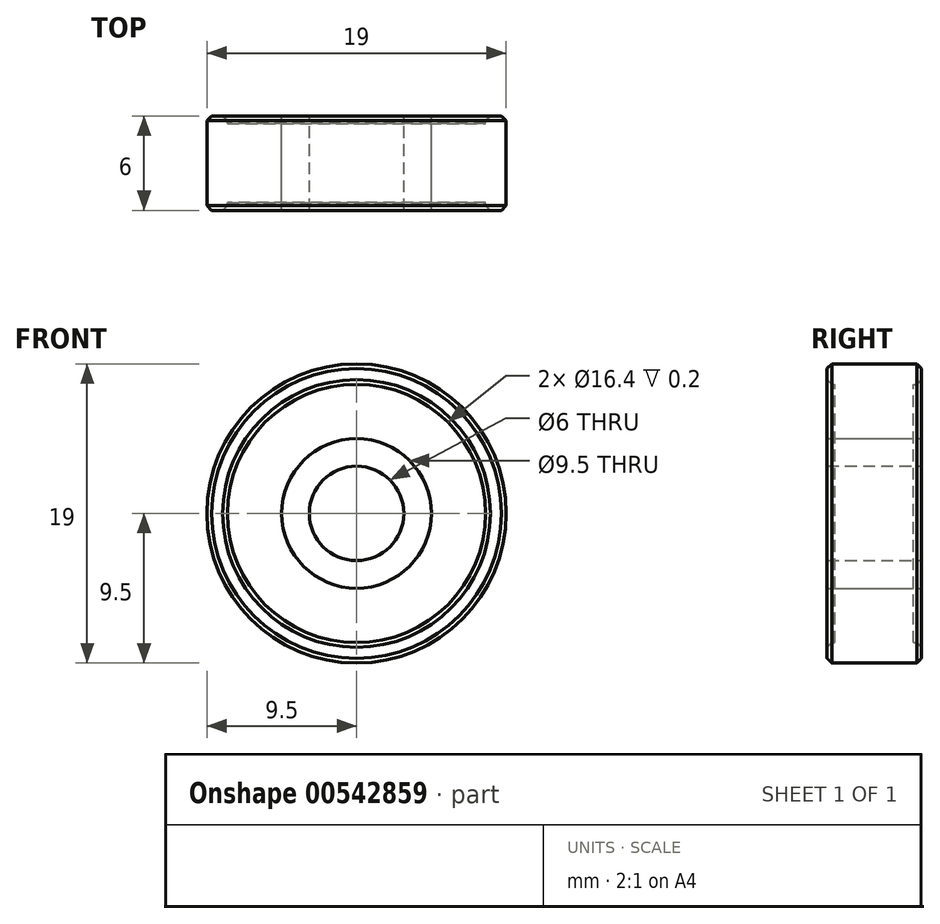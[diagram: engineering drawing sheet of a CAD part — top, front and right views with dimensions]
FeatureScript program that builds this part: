
annotation { "Feature Type Name" : "Feature", "Feature Type Description" : "" }
export const myFeature = defineFeature(function(context is Context, id is Id, definition is map)
    precondition{}
    {
        {
            var Q0;
            Q0=qCreatedBy(makeId("Front.planeOp"),FACE);
            var sketch = newSketch(context, id + "F0", { "sketchPlane" : qUnion([Q0])});
            skCircle(sketch, "E0", {"center": v(0, 0) * mm, "radius": 9.5 * mm});
            skCircle(sketch, "E1", {"center": v(0, 0) * mm, "radius": 8.2 * mm});
            skCircle(sketch, "E2", {"center": v(0, 0) * mm, "radius": 4.75 * mm});
            skCircle(sketch, "E3", {"center": v(0, 0) * mm, "radius": 3 * mm});
            skSolve(sketch);
        }
        {
            var Q0;
            Q0=makeQuery(id+"F0.imprint","IMPRINT",FACE,{"disambiguationData":[TD([[makeQuery(id+"F0.imprint","IMPRINT",EDGE,{"derivedFrom":sQuery(id+"F0.wireOp",EDGE,"E0")}),1.0]])]});
            extrude(context, id + "F1", {"entities" : qUnion([Q0]), "endBound" : BoundingType.SYMMETRIC, "depth" : 6 * mm, "offsetDistance" : 25 * mm});
        }
        {
            var Q0;
            Q0=makeQuery(id+"F0.imprint","IMPRINT",FACE,{"disambiguationData":[TD([[makeQuery(id+"F0.imprint","IMPRINT",EDGE,{"derivedFrom":sQuery(id+"F0.wireOp",EDGE,"E1")}),1.0]])]});
            extrude(context, id + "F2", {"entities" : qUnion([Q0]), "operationType" : NewBodyOperationType.ADD, "endBound" : BoundingType.SYMMETRIC, "depth" : 5 * mm});
        }
        {
            var Q0;
            Q0=makeQuery(id+"F1.opExtrude","CAP_FACE",FACE,{"disambiguationData":[OSD([sQuery(id+"F0.wireOp",EDGE,"E0"),sQuery(id+"F0.wireOp",EDGE,"E1")])],"isStart":false});
            var Q1;
            Q1=makeQuery(id+"F1.opExtrude","CAP_FACE",FACE,{"disambiguationData":[OSD([sQuery(id+"F0.wireOp",EDGE,"E2"),sQuery(id+"F0.wireOp",EDGE,"E3")])],"isStart":false});
            var Q2;
            Q2=makeQuery(id+"F1.opExtrude","CAP_FACE",FACE,{"disambiguationData":[OSD([sQuery(id+"F0.wireOp",EDGE,"E0"),sQuery(id+"F0.wireOp",EDGE,"E1")])],"isStart":true});
            var Q3;
            Q3=makeQuery(id+"F1.opExtrude","CAP_FACE",FACE,{"disambiguationData":[OSD([sQuery(id+"F0.wireOp",EDGE,"E2"),sQuery(id+"F0.wireOp",EDGE,"E3")])],"isStart":true});
            chamfer(context, id + "F3", {"entities" : qUnion([Q0, Q1, Q2, Q3]), "width" : .3 * mm, "tangentPropagation" : true});
        }
        {
            var Q0;
            Q0=makeQuery(id+"F0.imprint","IMPRINT",FACE,{"disambiguationData":[TD([[makeQuery(id+"F0.imprint","IMPRINT",EDGE,{"derivedFrom":sQuery(id+"F0.wireOp",EDGE,"E2")}),1.0]])]});
            extrude(context, id + "F4", {"entities" : qUnion([Q0]), "endBound" : BoundingType.SYMMETRIC, "depth" : 6 * mm, "offsetDistance" : 25 * mm});
        }
    });
